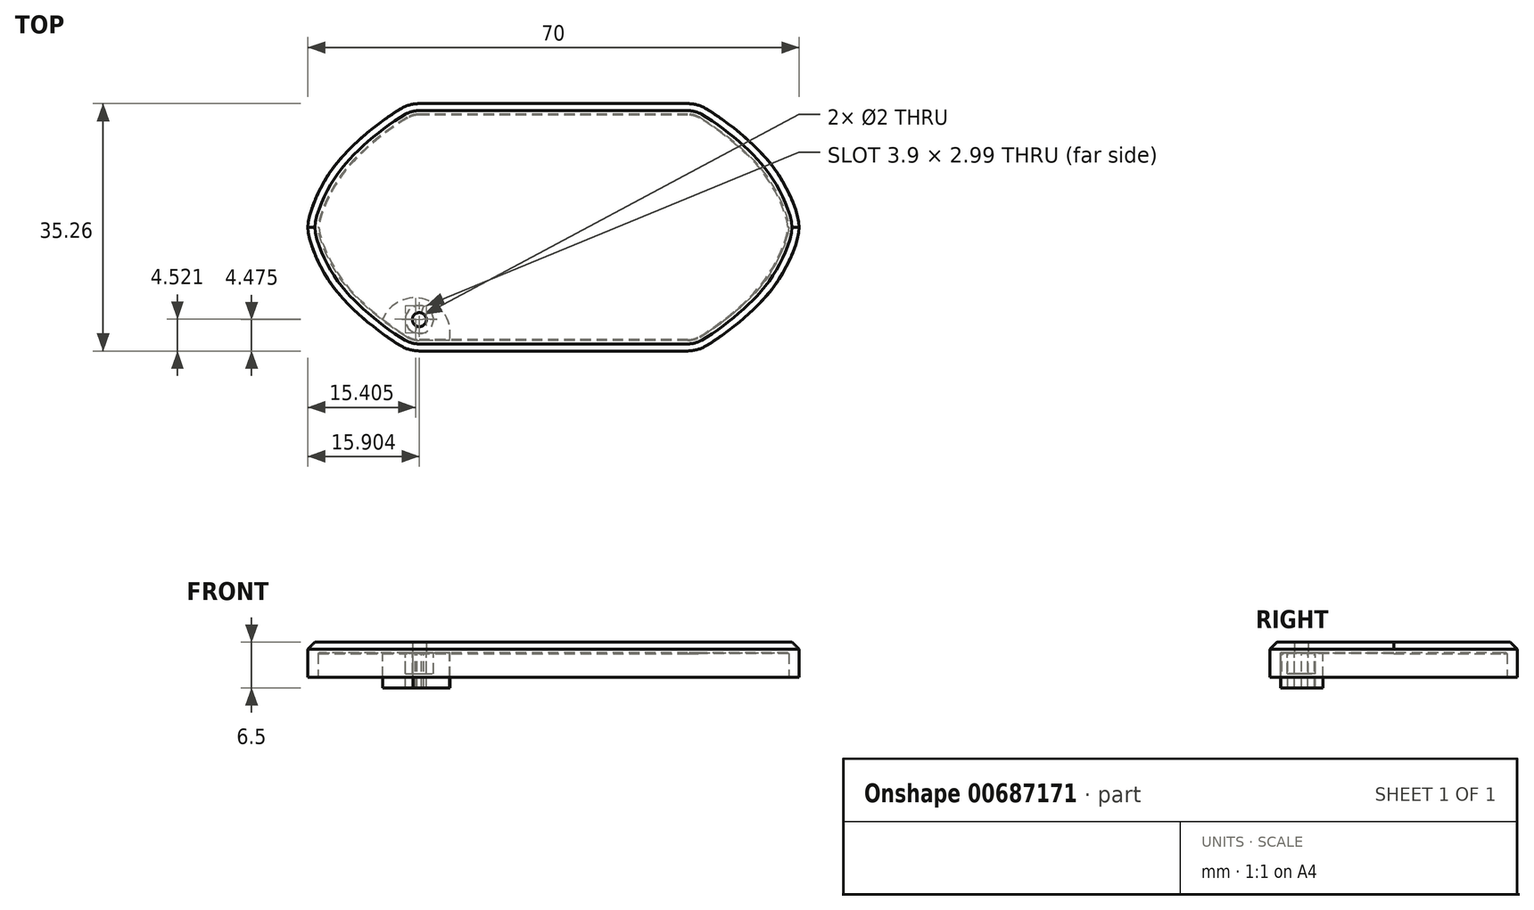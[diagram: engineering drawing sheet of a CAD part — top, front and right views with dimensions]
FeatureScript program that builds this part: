
annotation { "Feature Type Name" : "Feature", "Feature Type Description" : "" }
export const myFeature = defineFeature(function(context is Context, id is Id, definition is map)
    precondition{}
    {
        {
            var Q0;
            Q0=qCreatedBy(makeId("Top.planeOp"),FACE);
            var sketch = newSketch(context, id + "F0", { "sketchPlane" : qUnion([Q0])});
            skLineSegment(sketch, "E0.bottom", {"start": v(0, 17.62) * mm, "end": v(-20, 17.62) * mm});
            skLineSegment(sketch, "E0.top", {"start": v(0, -17.62) * mm, "end": v(-20, -17.62) * mm});
            skLineSegment(sketch, "E0.right", {"start": v(-20, 17.62) * mm, "end": v(-20, -17.62) * mm});
            skPoint(sketch, "E0.middle", {"position": v(0, 0) * mm});
            skFitSpline(sketch, "E1", {"points": [v(-20, 17.62) * mm, v(-24.04, 15.37) * mm, v(-29.04, 11.16) * mm, v(-32.7, 6.43) * mm, v(-35, 0) * mm], "startDerivative": vector(-10.03, -0.46) * mm, "endDerivative": vector(0, -18.64) * mm});
            skLineSegment(sketch, "E2", {"start": v(-35, 0) * mm, "end": v(-35, 14.78) * mm, "construction": true});
            skLineSegment(sketch, "E3", {"start": v(-35, 0) * mm, "end": v(0, 0) * mm, "construction": true});
            skFitSpline(sketch, "E4.MirrorCS", {"points": [v(-20, -17.62) * mm, v(-24.04, -15.37) * mm, v(-29.04, -11.16) * mm, v(-32.7, -6.43) * mm, v(-35, 0) * mm], "startDerivative": vector(-10.03, 0.46) * mm, "endDerivative": vector(0, 18.64) * mm});
            skLineSegment(sketch, "E5", {"start": v(0, 17.62) * mm, "end": v(0, -17.62) * mm});
            skPoint(sketch, "E6.orphan", {"position": v(20, 17.62) * mm});
            skPoint(sketch, "E7.orphan", {"position": v(20, -17.62) * mm});
            skSolve(sketch);
        }
        {
            var Q0;
            Q0=makeQuery(id+"F0.imprint","IMPRINT",FACE,{"disambiguationData":[TD([[makeQuery(id+"F0.imprint","IMPRINT",EDGE,{"derivedFrom":sQuery(id+"F0.wireOp",EDGE,"E0.bottom")}),1.0]])]});
            var Q1;
            Q1=makeQuery(id+"F0.imprint","IMPRINT",FACE,{"disambiguationData":[TD([[makeQuery(id+"F0.imprint","IMPRINT",EDGE,{"derivedFrom":sQuery(id+"F0.wireOp",EDGE,"E0.right")}),-1.0]])]});
            extrude(context, id + "F1", {"entities" : qUnion([Q0, Q1]), "endBound" : BoundingType.SYMMETRIC, "depth" : 5 * mm, "offsetDistance" : 25 * mm});
        }
        {
            var Q0;
            Q0=makeQuery(id+"F1.opExtrude","SWEPT_EDGE",EDGE,{"disambiguationData":[OSD([sQuery(id+"F0.wireOp",EDGE,"E0.bottom"),sQuery(id+"F0.wireOp",EDGE,"E0.right"),sQuery(id+"F0.wireOp",EDGE,"E1")])]});
            var Q1;
            Q1=makeQuery(id+"F3.opPattern","COPY",EDGE,{"derivedFrom":makeQuery(id+"F1.opExtrude","SWEPT_EDGE",EDGE,{"disambiguationData":[OSD([sQuery(id+"F0.wireOp",EDGE,"E0.bottom"),sQuery(id+"F0.wireOp",EDGE,"E0.right"),sQuery(id+"F0.wireOp",EDGE,"E1")])]}),"instanceName":"1"});
            var Q2;
            Q2=makeQuery(id+"F1.opExtrude","SWEPT_EDGE",EDGE,{"disambiguationData":[OSD([sQuery(id+"F0.wireOp",EDGE,"E0.top"),sQuery(id+"F0.wireOp",EDGE,"E0.right"),sQuery(id+"F0.wireOp",EDGE,"E4.MirrorCS")])]});
            var Q3;
            Q3=makeQuery(id+"F3.opPattern","COPY",EDGE,{"derivedFrom":makeQuery(id+"F1.opExtrude","SWEPT_EDGE",EDGE,{"disambiguationData":[OSD([sQuery(id+"F0.wireOp",EDGE,"E0.top"),sQuery(id+"F0.wireOp",EDGE,"E0.right"),sQuery(id+"F0.wireOp",EDGE,"E4.MirrorCS")])]}),"instanceName":"1"});
            fillet(context, id + "F2", {"entities" : qUnion([Q0, Q1, Q2, Q3]), "radius" : 5 * mm, "tangentPropagation" : true, "allowEdgeOverflow" : false});
        }
        {
            var Q0;
            Q0=makeQuery(id+"F1.opExtrude","SWEPT_BODY",BODY,{"disambiguationData":[OSD([sQuery(id+"F0.wireOp",EDGE,"E0.bottom"),sQuery(id+"F0.wireOp",EDGE,"E0.top"),sQuery(id+"F0.wireOp",EDGE,"E1"),sQuery(id+"F0.wireOp",EDGE,"E4.MirrorCS"),sQuery(id+"F0.wireOp",EDGE,"E5")])]});
            var Q1;
            Q1=makeQuery(id+"F1.opExtrude","SWEPT_FACE",FACE,{"disambiguationData":[OSD([sQuery(id+"F0.wireOp",EDGE,"E5")])]});
            mirror(context, id + "F3", {"operationType" : NewBodyOperationType.ADD, "entities" : qUnion([Q0]), "mirrorPlane" : qUnion([Q1])});
        }
        {
            var Q0;
            {var subQ0=makeQuery(id+"F1.opExtrude","CAP_EDGE",EDGE,{"disambiguationData":[OSD([sQuery(id+"F0.wireOp",EDGE,"E0.top")])],"isStart":false});Q0=makeQuery(id+"F3.boolean.opBoolean","MERGE",EDGE,{"derivedFrom":[subQ0,makeQuery(id+"F3.opPattern","COPY",EDGE,{"derivedFrom":subQ0,"instanceName":"1"})]});}
            var Q1;
            Q1=makeQuery(id+"FhYhS6fhlekAtoq_2.splitOp","SPLIT_SURFACE_INTERSECT",EDGE,{"derivedFrom":[makeQuery(id+"F1.opExtrude","SWEPT_FACE",FACE,{"disambiguationData":[OSD([sQuery(id+"F0.wireOp",EDGE,"E4.MirrorCS")])]})]});
            var Q2;
            Q2=makeQuery(id+"F3.opPattern","COPY",EDGE,{"derivedFrom":makeQuery(id+"FhYhS6fhlekAtoq_2.splitOp","SPLIT_SURFACE_INTERSECT",EDGE,{"derivedFrom":[makeQuery(id+"F1.opExtrude","SWEPT_FACE",FACE,{"disambiguationData":[OSD([sQuery(id+"F0.wireOp",EDGE,"E4.MirrorCS")])]})]}),"instanceName":"1"});
            var Q3;
            {var subQ0=makeQuery(id+"F1.opExtrude","CAP_EDGE",EDGE,{"disambiguationData":[OSD([sQuery(id+"F0.wireOp",EDGE,"E0.bottom")])],"isStart":false});Q3=makeQuery(id+"F3.boolean.opBoolean","MERGE",EDGE,{"derivedFrom":[subQ0,makeQuery(id+"F3.opPattern","COPY",EDGE,{"derivedFrom":subQ0,"instanceName":"1"})]});}
            chamfer(context, id + "F4", {"entities" : qUnion([Q0, Q1, Q2, Q3]), "width" : 1 * mm, "tangentPropagation" : true});
        }
        {
            var Q0;
            {var subQ0=makeQuery(id+"F1.opExtrude","CAP_FACE",FACE,{"disambiguationData":[OSD([sQuery(id+"F0.wireOp",EDGE,"E0.bottom"),sQuery(id+"F0.wireOp",EDGE,"E0.top"),sQuery(id+"F0.wireOp",EDGE,"E1"),sQuery(id+"F0.wireOp",EDGE,"E4.MirrorCS"),sQuery(id+"F0.wireOp",EDGE,"E5")])],"isStart":true});Q0=makeQuery(id+"F3.boolean.opBoolean","MERGE",FACE,{"derivedFrom":[subQ0,makeQuery(id+"F3.opPattern","COPY",FACE,{"derivedFrom":subQ0,"instanceName":"1"})]});}
            shell(context, id + "F5", {"entities" : qUnion([Q0]), "thickness" : 1.5 * mm});
        }
        {
            var Q0;
            Q0=makeQuery(id+"F5.opShell","OFFSET_FACE",FACE,{"disambiguationData":[OSD([sQuery(id+"F0.wireOp",EDGE,"E0.bottom"),sQuery(id+"F0.wireOp",EDGE,"E0.top"),sQuery(id+"F0.wireOp",EDGE,"E1"),sQuery(id+"F0.wireOp",EDGE,"E4.MirrorCS"),sQuery(id+"F0.wireOp",EDGE,"E5")])]});
            var sketch = newSketch(context, id + "F6", { "sketchPlane" : qUnion([Q0])});
            skArc(sketch, "E8", {"start": v(-24.38, 13.25) * mm, "mid": v(-18.27, 10.27) * mm, "end": v(-14.82, 16.12) * mm});
            skCircle(sketch, "E9", {"center": v(-19.1, 13.15) * mm, "radius": 1 * mm});
            skArc(sketch, "E10.0", {"start": v(-19.13, 16.13) * mm, "mid": v(-20.02, 16) * mm, "end": v(-20.86, 15.67) * mm});
            skFitSpline(sketch, "E10.1", {"points": [v(-20.86, 15.67) * mm, v(-21.23, 15.45) * mm, v(-21.97, 15) * mm, v(-23.39, 14) * mm, v(-24.77, 12.97) * mm, v(-26.1, 11.86) * mm, v(-27.06, 11) * mm, v(-27.99, 10.1) * mm, v(-28.88, 9.17) * mm, v(-29.71, 8.2) * mm, v(-30.49, 7.16) * mm, v(-31.2, 6.05) * mm, v(-31.83, 4.91) * mm, v(-32.4, 3.74) * mm, v(-32.82, 2.74) * mm, v(-33.11, 1.91) * mm, v(-33.3, 1.29) * mm, v(-33.44, 0.66) * mm, v(-33.5, 0.22) * mm, v(-33.5, 0) * mm]});
            skLineSegment(sketch, "E10.2", {"start": v(-14.82, 16.12) * mm, "end": v(-19.13, 16.12) * mm});
            skPoint(sketch, "E11.orphan", {"position": v(-33.5, 0) * mm});
            skPoint(sketch, "E12.orphan", {"position": v(19.13, 16.12) * mm});
            skLineSegment(sketch, "E13", {"start": v(-20.02, 16) * mm, "end": v(-18.17, 10.3) * mm});
            skLineSegment(sketch, "E14", {"start": v(-20.02, 16) * mm, "end": v(-19.72, 15.06) * mm});
            skCircle(sketch, "E15", {"center": v(-19.1, 13.15) * mm, "radius": 2 * mm});
            skSolve(sketch);
        }
        {
            var Q0;
            Q0=makeQuery(id+"F6.imprint","IMPRINT",FACE,{"disambiguationData":[TD([[makeQuery(id+"F6.imprint","IMPRINT",EDGE,{"derivedFrom":sQuery(id+"F6.wireOp",EDGE,"E10.0")}),1.0]])]});
            var Q1;
            {var subQ0=sQuery(id+"F0.wireOp",EDGE,"E5");var subQ1=sQuery(id+"F0.wireOp",EDGE,"E4.MirrorCS");var subQ2=sQuery(id+"F0.wireOp",EDGE,"E1");var subQ3=sQuery(id+"F0.wireOp",EDGE,"E0.top");var subQ4=sQuery(id+"F0.wireOp",EDGE,"E0.bottom");var subQ5=makeQuery(id+"F1.opExtrude","CAP_FACE",FACE,{"disambiguationData":[OSD([subQ4,subQ3,subQ2,subQ1,subQ0])],"isStart":false});var subQ6=subQ5;var subQ7=makeQuery(id+"FhYhS6fhlekAtoq_2.splitOp","SPLIT",FACE,{"derivedFrom":subQ6});var subQ8=makeQuery(id+"F3.boolean.opBoolean","MERGE",FACE,{"derivedFrom":[subQ7,makeQuery(id+"F3.opPattern","COPY",FACE,{"derivedFrom":subQ7,"instanceName":"1"})]});var subQ9=sQuery(id+"F0.wireOp",EDGE,"E0.right");var subQ15=makeQuery(id+"F5.opShell","OFFSET_EDGE",EDGE,{"disambiguationData":[OSD([subQ4,subQ3,subQ9,subQ2,subQ1,subQ0]),TDD([makeQuery(id+"F4.opChamfer","BLEND_EDGE",EDGE,{"blendedFrom":[makeQuery(id+"FhYhS6fhlekAtoq_2.splitOp","SPLIT",EDGE,{"derivedFrom":makeQuery(id+"F2.opFillet","BLEND_EDGE",EDGE,{"blendedFrom":[makeQuery(id+"F1.opExtrude","SWEPT_EDGE",EDGE,{"disambiguationData":[OSD([subQ3,subQ9,subQ1])]}),subQ5],"blendedInto":[subQ5]})}),subQ8],"blendedInto":[subQ8]})])]});Q1=makeQuery(id+"F6.imprint","IMPRINT",FACE,{"disambiguationData":[TD([[makeQuery(id+"F6.imprint","IMPRINT",EDGE,{"derivedFrom":subQ15}),-1.0]])]});}
            var Q2;
            {var subQ0=sQuery(id+"F6.wireOp",EDGE,"E14");var subQ1=sQuery(id+"F6.wireOp",EDGE,"E13");var subQ2=makeQuery(id+"F6.imprint","INTERSECT",VERTEX,{"derivedFrom":[subQ1,subQ0]});Q2=makeQuery(id+"F6.imprint","IMPRINT",FACE,{"disambiguationData":[TD([[makeQuery(id+"F6.imprint","IMPRINT",EDGE,{"disambiguationData":[TD([[subQ2,-1.0]])],"derivedFrom":subQ1}),1.0]])]});}
            var Q3;
            {var subQ0=sQuery(id+"F6.wireOp",EDGE,"E10.1");Q3=makeQuery(id+"F6.imprint","IMPRINT",FACE,{"disambiguationData":[TD([[makeQuery(id+"F6.imprint","IMPRINT",EDGE,{"derivedFrom":subQ0}),1.0]])]});}
            var Q4;
            {var subQ0=sQuery(id+"F6.wireOp",EDGE,"E13");var subQ1=sQuery(id+"F6.wireOp",EDGE,"E8");var subQ2=makeQuery(id+"F6.imprint","INTERSECT",VERTEX,{"derivedFrom":[subQ1,subQ0]});Q4=makeQuery(id+"F6.imprint","IMPRINT",FACE,{"disambiguationData":[TD([[makeQuery(id+"F6.imprint","IMPRINT",EDGE,{"disambiguationData":[TD([[subQ2,1.0]])],"derivedFrom":subQ0}),-1.0]])]});}
            extrude(context, id + "F7", {"entities" : qUnion([Q0, Q1, Q2, Q3, Q4]), "depth" : 5 * mm, "offsetDistance" : 25 * mm});
        }
        {
            var Q0;
            {var subQ0=sQuery(id+"F6.wireOp",EDGE,"E13");var subQ1=sQuery(id+"F6.wireOp",EDGE,"E9");var subQ2=makeQuery(id+"F6.imprint","INTERSECT",VERTEX,{"disambiguationData":[OD(0.0)],"derivedFrom":[subQ1,subQ0]});Q0=makeQuery(id+"F6.imprint","IMPRINT",FACE,{"disambiguationData":[TD([[makeQuery(id+"F6.imprint","IMPRINT",EDGE,{"disambiguationData":[TD([[subQ2,1.0]])],"derivedFrom":subQ1}),1.0]])]});}
            var Q1;
            {var subQ0=sQuery(id+"F6.wireOp",EDGE,"E13");var subQ1=sQuery(id+"F6.wireOp",EDGE,"E9");var subQ2=makeQuery(id+"F6.imprint","INTERSECT",VERTEX,{"disambiguationData":[OD(0.0)],"derivedFrom":[subQ1,subQ0]});Q1=makeQuery(id+"F6.imprint","IMPRINT",FACE,{"disambiguationData":[TD([[makeQuery(id+"F6.imprint","IMPRINT",EDGE,{"disambiguationData":[TD([[subQ2,-1.0]])],"derivedFrom":subQ1}),1.0]])]});}
            extrude(context, id + "F8", {"entities" : qUnion([Q0, Q1]), "operationType" : NewBodyOperationType.REMOVE, "oppositeDirection" : true, "depth" : 25 * mm, "offsetDistance" : 25 * mm});
        }
        {
            var Q0;
            {var subQ0=sQuery(id+"F6.wireOp",EDGE,"E13");var subQ1=sQuery(id+"F6.wireOp",EDGE,"E9");var subQ2=makeQuery(id+"F6.imprint","INTERSECT",VERTEX,{"disambiguationData":[OD(0.0)],"derivedFrom":[subQ1,subQ0]});Q0=makeQuery(id+"F6.imprint","IMPRINT",FACE,{"disambiguationData":[TD([[makeQuery(id+"F6.imprint","IMPRINT",EDGE,{"disambiguationData":[TD([[subQ2,1.0]])],"derivedFrom":subQ1}),-1.0]])]});}
            var Q1;
            {var subQ1=sQuery(id+"F6.wireOp",EDGE,"E13");var subQ10=sQuery(id+"F6.wireOp",EDGE,"E9");var subQ13=makeQuery(id+"F6.imprint","INTERSECT",VERTEX,{"disambiguationData":[OD(0.0)],"derivedFrom":[subQ10,subQ1]});Q1=makeQuery(id+"F6.imprint","IMPRINT",FACE,{"disambiguationData":[TD([[makeQuery(id+"F6.imprint","IMPRINT",EDGE,{"disambiguationData":[TD([[subQ13,-1.0]])],"derivedFrom":subQ10}),-1.0]])]});}
            var Q2;
            {var subQ0=sQuery(id+"F6.wireOp",EDGE,"E15");var subQ1=sQuery(id+"F0.wireOp",EDGE,"E5");var subQ2=sQuery(id+"F0.wireOp",EDGE,"E4.MirrorCS");var subQ3=sQuery(id+"F0.wireOp",EDGE,"E1");var subQ4=sQuery(id+"F0.wireOp",EDGE,"E0.top");var subQ5=sQuery(id+"F0.wireOp",EDGE,"E0.bottom");var subQ6=makeQuery(id+"F5.opShell","OFFSET_EDGE",EDGE,{"disambiguationData":[OSD([subQ5,subQ4,subQ3,subQ2,subQ1]),TDD([makeQuery(id+"FhYhS6fhlekAtoq_2.splitOp","SPLIT_SURFACE_INTERSECT",EDGE,{"derivedFrom":[makeQuery(id+"F1.opExtrude","CAP_FACE",FACE,{"disambiguationData":[OSD([subQ5,subQ4,subQ3,subQ2,subQ1])],"isStart":false})]})])]});var subQ7=makeQuery(id+"F6.imprint","INTERSECT",VERTEX,{"disambiguationData":[OD(0.0)],"derivedFrom":[subQ6,subQ0]});Q2=makeQuery(id+"F6.imprint","IMPRINT",FACE,{"disambiguationData":[TD([[makeQuery(id+"F6.imprint","IMPRINT",EDGE,{"disambiguationData":[TD([[subQ7,-1.0]])],"derivedFrom":subQ0}),1.0]])]});}
            extrude(context, id + "F9", {"entities" : qUnion([Q0, Q1, Q2]), "depth" : 3 * mm, "offsetDistance" : 25 * mm});
        }
    });
